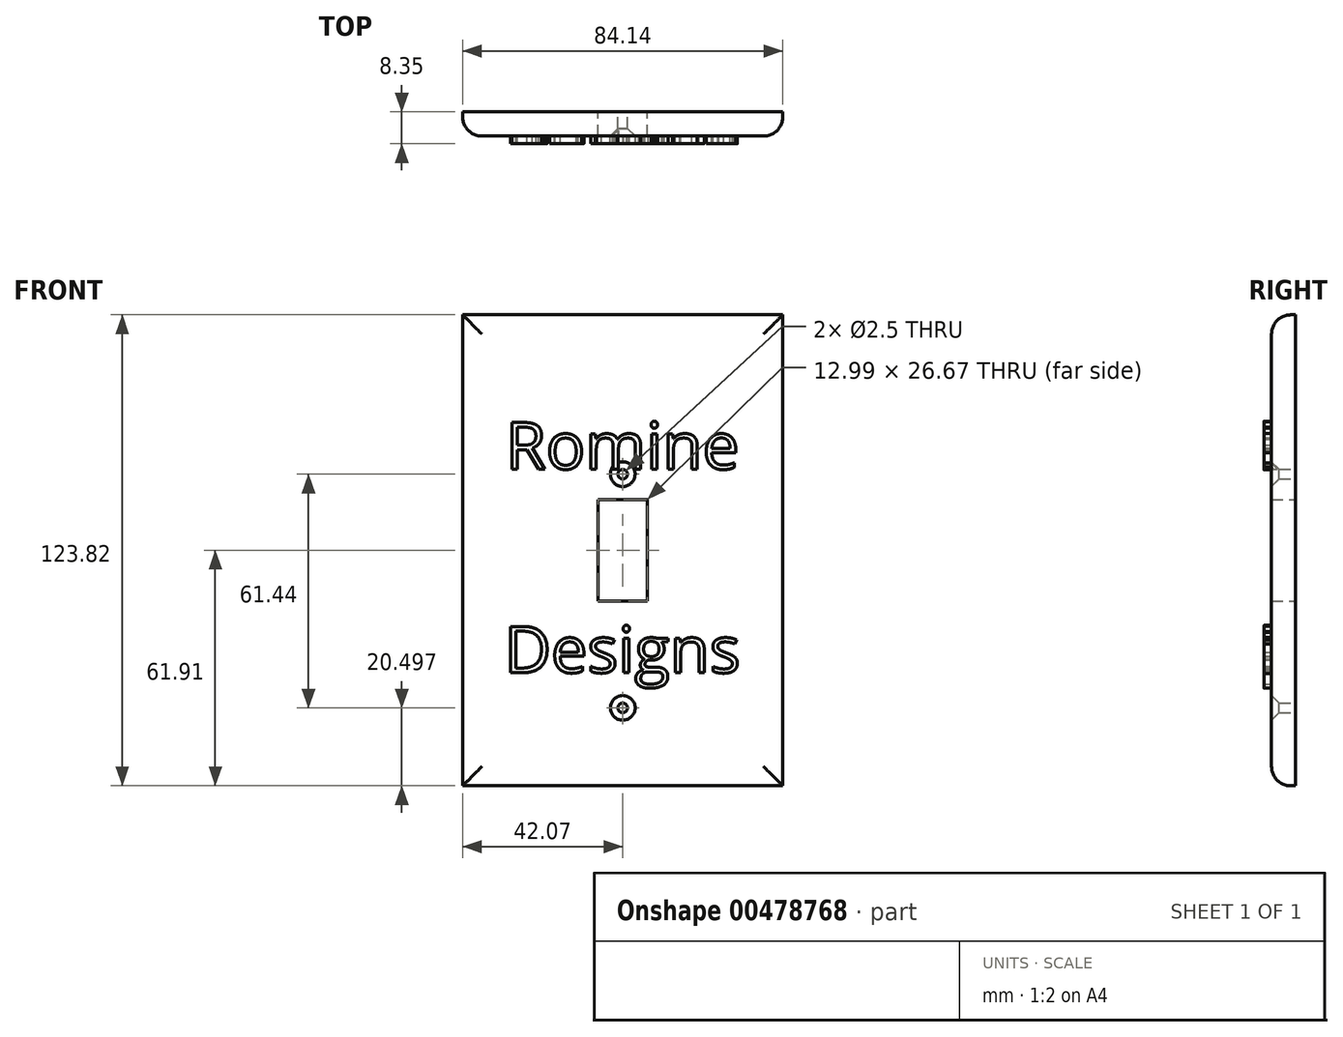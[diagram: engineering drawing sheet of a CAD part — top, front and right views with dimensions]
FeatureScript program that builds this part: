
annotation { "Feature Type Name" : "Feature", "Feature Type Description" : "" }
export const myFeature = defineFeature(function(context is Context, id is Id, definition is map)
    precondition{}
    {
        {
            var Q0;
            Q0=qCreatedBy(makeId("Front.planeOp"),FACE);
            var sketch = newSketch(context, id + "F0", { "sketchPlane" : qUnion([Q0])});
            skLineSegment(sketch, "E0.bottom", {"start": v(-42.07, 61.91) * mm, "end": v(42.07, 61.91) * mm});
            skLineSegment(sketch, "E0.top", {"start": v(-42.07, -61.91) * mm, "end": v(42.07, -61.91) * mm});
            skLineSegment(sketch, "E0.left", {"start": v(-42.07, 61.91) * mm, "end": v(-42.07, -61.91) * mm});
            skLineSegment(sketch, "E0.right", {"start": v(42.07, 61.91) * mm, "end": v(42.07, -61.91) * mm});
            skPoint(sketch, "E0.middle", {"position": v(0, 0) * mm});
            skLineSegment(sketch, "E1.bottom", {"start": v(-6.5, 13.33) * mm, "end": v(6.5, 13.33) * mm});
            skLineSegment(sketch, "E1.top", {"start": v(-6.5, -13.33) * mm, "end": v(6.5, -13.33) * mm});
            skLineSegment(sketch, "E1.left", {"start": v(-6.5, 13.33) * mm, "end": v(-6.5, -13.33) * mm});
            skLineSegment(sketch, "E1.right", {"start": v(6.5, 13.33) * mm, "end": v(6.5, -13.33) * mm});
            skLineSegment(sketch, "E2", {"start": v(0, 0) * mm, "end": v(0, 20.03) * mm});
            skPoint(sketch, "E2.endSnap0", {"position": v(0, 13.33) * mm});
            skLineSegment(sketch, "E3", {"start": v(0, 20.03) * mm, "end": v(0, -41.41) * mm});
            skCircle(sketch, "E4", {"center": v(0, 20.03) * mm, "radius": 1.25 * mm});
            skCircle(sketch, "E5", {"center": v(0, -41.41) * mm, "radius": 1.25 * mm});
            skSolve(sketch);
        }
        {
            var Q0;
            Q0=makeQuery(id+"F0.imprint","IMPRINT",FACE,{"disambiguationData":[TD([[makeQuery(id+"F0.imprint","IMPRINT",EDGE,{"derivedFrom":sQuery(id+"F0.wireOp",EDGE,"E0.bottom")}),-1.0]])]});
            var Q1;
            Q1=makeQuery(id+"F0.imprint","IMPRINT",FACE,{"disambiguationData":[TD([[makeQuery(id+"F0.imprint","IMPRINT",EDGE,{"derivedFrom":sQuery(id+"F0.wireOp",EDGE,"5d08ede4-09dc-498b-8d78-4f409da95cb2.sketch_text.stroke-7")}),1.0]])]});
            var Q2;
            Q2=makeQuery(id+"F0.imprint","IMPRINT",FACE,{"disambiguationData":[TD([[makeQuery(id+"F0.imprint","IMPRINT",EDGE,{"derivedFrom":sQuery(id+"F0.wireOp",EDGE,"5d08ede4-09dc-498b-8d78-4f409da95cb2.sketch_text.stroke-28")}),1.0]])]});
            var Q3;
            Q3=makeQuery(id+"F0.imprint","IMPRINT",FACE,{"disambiguationData":[TD([[makeQuery(id+"F0.imprint","IMPRINT",EDGE,{"derivedFrom":sQuery(id+"F0.wireOp",EDGE,"5d08ede4-09dc-498b-8d78-4f409da95cb2.sketch_text.stroke-108")}),1.0]])]});
            var Q4;
            Q4=makeQuery(id+"F0.imprint","IMPRINT",FACE,{"disambiguationData":[TD([[makeQuery(id+"F0.imprint","IMPRINT",EDGE,{"derivedFrom":sQuery(id+"F0.wireOp",EDGE,"5d08ede4-09dc-498b-8d78-4f409da95cb2.sketch_text.stroke-99")}),1.0]])]});
            var Q5;
            Q5=makeQuery(id+"F0.imprint","IMPRINT",FACE,{"disambiguationData":[TD([[makeQuery(id+"F0.imprint","IMPRINT",EDGE,{"derivedFrom":sQuery(id+"F0.wireOp",EDGE,"f573bca0-283b-481b-9769-5f4718476758.sketch_text.stroke-11")}),1.0]])]});
            var Q6;
            Q6=makeQuery(id+"F0.imprint","IMPRINT",FACE,{"disambiguationData":[TD([[makeQuery(id+"F0.imprint","IMPRINT",EDGE,{"derivedFrom":sQuery(id+"F0.wireOp",EDGE,"f573bca0-283b-481b-9769-5f4718476758.sketch_text.stroke-27")}),1.0]])]});
            var Q7;
            Q7=makeQuery(id+"F0.imprint","IMPRINT",FACE,{"disambiguationData":[TD([[makeQuery(id+"F0.imprint","IMPRINT",EDGE,{"derivedFrom":sQuery(id+"F0.wireOp",EDGE,"f573bca0-283b-481b-9769-5f4718476758.sketch_text.stroke-106")}),1.0]])]});
            extrude(context, id + "F1", {"entities" : qUnion([Q0, Q1, Q2, Q3, Q4, Q5, Q6, Q7]), "depth" : 6.35 * mm});
        }
        {
            var Q0;
            Q0=makeQuery(id+"F1.opExtrude","CAP_EDGE",EDGE,{"disambiguationData":[OSD([sQuery(id+"F0.wireOp",EDGE,"E0.left")])],"isStart":false});
            var Q1;
            Q1=makeQuery(id+"F1.opExtrude","CAP_EDGE",EDGE,{"disambiguationData":[OSD([sQuery(id+"F0.wireOp",EDGE,"E0.right")])],"isStart":false});
            var Q2;
            Q2=makeQuery(id+"F1.opExtrude","CAP_EDGE",EDGE,{"disambiguationData":[OSD([sQuery(id+"F0.wireOp",EDGE,"E0.top")])],"isStart":false});
            var Q3;
            Q3=makeQuery(id+"F1.opExtrude","CAP_EDGE",EDGE,{"disambiguationData":[OSD([sQuery(id+"F0.wireOp",EDGE,"E0.bottom")])],"isStart":false});
            fillet(context, id + "F2", {"entities" : qUnion([Q0, Q1, Q2, Q3]), "radius" : 5.08 * mm, "tangentPropagation" : true, "allowEdgeOverflow" : false});
        }
        {
            var Q0;
            Q0=makeQuery(id+"F1.opExtrude","CAP_FACE",FACE,{"disambiguationData":[OSD([sQuery(id+"F0.wireOp",EDGE,"E0.bottom"),sQuery(id+"F0.wireOp",EDGE,"E0.top"),sQuery(id+"F0.wireOp",EDGE,"E0.left"),sQuery(id+"F0.wireOp",EDGE,"E0.right"),sQuery(id+"F0.wireOp",EDGE,"E1.bottom"),sQuery(id+"F0.wireOp",EDGE,"E1.top"),sQuery(id+"F0.wireOp",EDGE,"E1.left"),sQuery(id+"F0.wireOp",EDGE,"E1.right")])],"isStart":false});
            var sketch = newSketch(context, id + "F3", { "sketchPlane" : qUnion([Q0])});
            skText(sketch, "E6", { "text": "Romine\n", "fontName": "OpenSans-Regular.ttf"});
            skText(sketch, "E7", { "text": "Designs\n", "fontName": "OpenSans-Regular.ttf"});
            const initialGuessF3  = {"E6": [-0.03077, 0.02137, 1, 0, 0.01234], "E7": [-0.0312, -0.03216, 1, 0, 0.01222]};
            skSetInitialGuess(sketch, initialGuessF3);
            skSolve(sketch);
        }
        {
            var Q0;
            Q0 = qSketchRegion(id + "F3", true);
            extrude(context, id + "F4", {"entities" : qUnion([Q0]), "operationType" : NewBodyOperationType.ADD, "depth" : 2 * mm});
        }
        {
            var Q0;
            Q0=makeQuery(id+"F1.opExtrude","CAP_EDGE",EDGE,{"disambiguationData":[OSD([sQuery(id+"F0.wireOp",EDGE,"E4")])],"isStart":false});
            var Q1;
            Q1=makeQuery(id+"F1.opExtrude","CAP_EDGE",EDGE,{"disambiguationData":[OSD([sQuery(id+"F0.wireOp",EDGE,"E5")])],"isStart":false});
            chamfer(context, id + "F5", {"entities" : qUnion([Q0, Q1]), "width" : 2 * mm, "tangentPropagation" : true});
        }
    });
